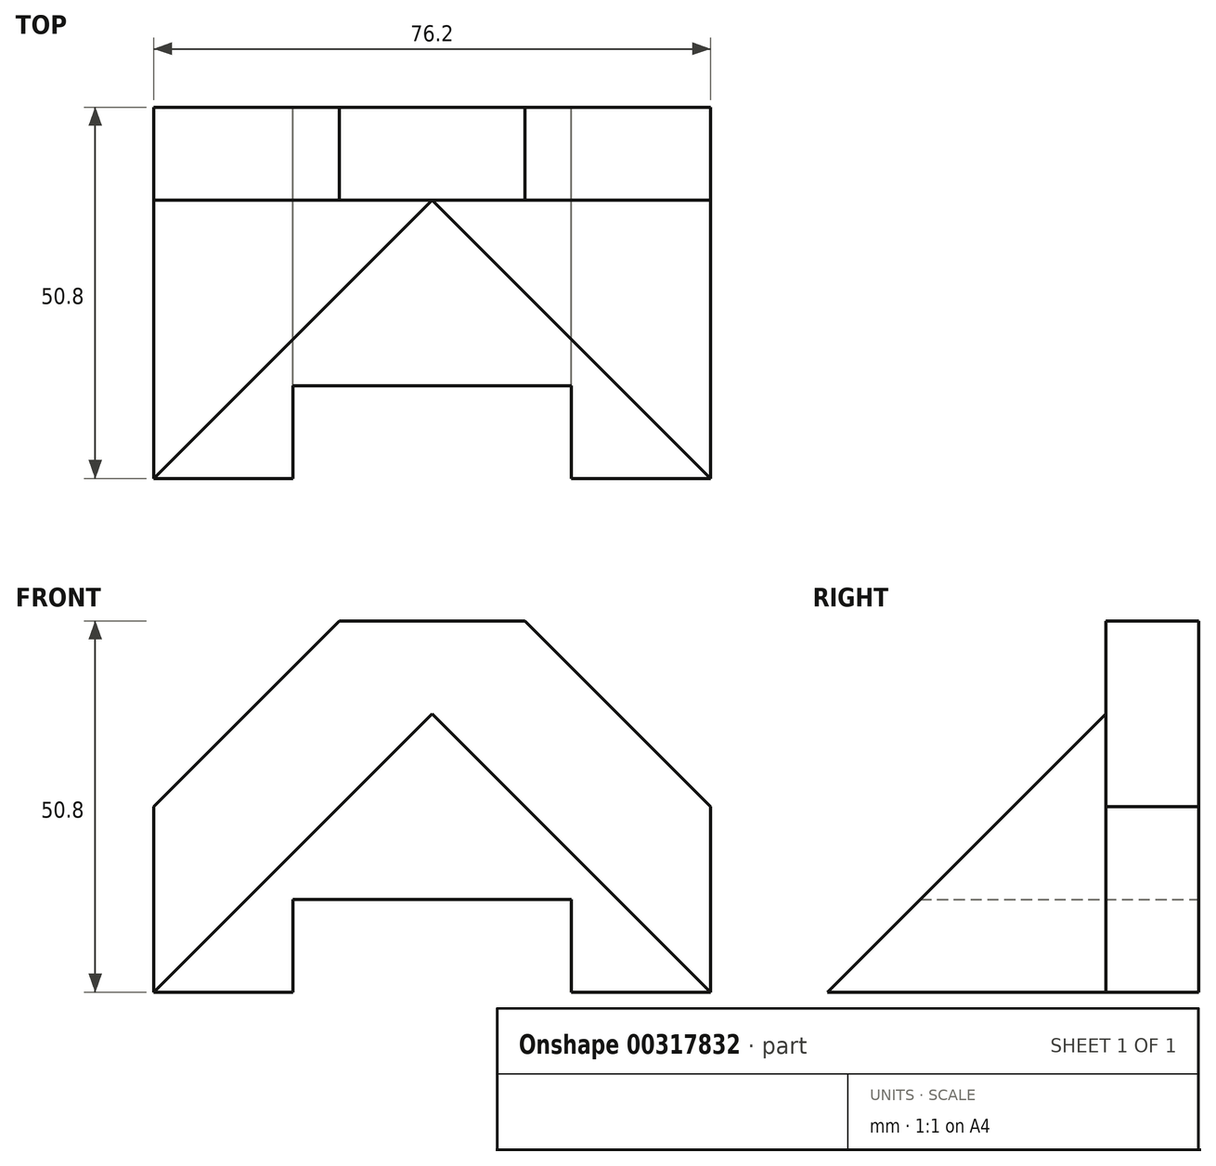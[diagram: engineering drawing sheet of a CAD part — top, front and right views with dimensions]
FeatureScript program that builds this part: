
annotation { "Feature Type Name" : "Feature", "Feature Type Description" : "" }
export const myFeature = defineFeature(function(context is Context, id is Id, definition is map)
    precondition{}
    {
        {
            var Q0;
            Q0=qCreatedBy(makeId("Top.planeOp"),FACE);
            var sketch = newSketch(context, id + "F0", { "sketchPlane" : qUnion([Q0])});
            skLineSegment(sketch, "E0", {"start": v(0, 0) * mm, "end": v(0, 50.8) * mm});
            skLineSegment(sketch, "E1", {"start": v(0, 50.8) * mm, "end": v(76.2, 50.8) * mm});
            skLineSegment(sketch, "E2", {"start": v(76.2, 50.8) * mm, "end": v(76.2, 0) * mm});
            skLineSegment(sketch, "E3", {"start": v(76.2, 0) * mm, "end": v(0, 0) * mm});
            skLineSegment(sketch, "E4", {"start": v(0, 38.1) * mm, "end": v(76.2, 38.1) * mm});
            skSolve(sketch);
        }
        {
            var Q0;
            {var subQ0=sQuery(id+"F0.wireOp",EDGE,"E1");Q0=makeQuery(id+"F0.imprint","IMPRINT",FACE,{"disambiguationData":[TD([[makeQuery(id+"F0.imprint","IMPRINT",EDGE,{"derivedFrom":subQ0}),-1.0]])]});}
            extrude(context, id + "F1", {"entities" : qUnion([Q0]), "depth" : 50.8 * mm});
        }
        {
            var Q0;
            Q0=makeQuery(id+"F1.opExtrude","SWEPT_FACE",FACE,{"disambiguationData":[OSD([sQuery(id+"F0.wireOp",EDGE,"E1")])]});
            var sketch = newSketch(context, id + "F2", { "sketchPlane" : qUnion([Q0])});
            skLineSegment(sketch, "E5", {"start": v(-25.4, 50.8) * mm, "end": v(0, 25.4) * mm});
            skLineSegment(sketch, "E6", {"start": v(0, 25.4) * mm, "end": v(0, 50.8) * mm});
            skLineSegment(sketch, "E7", {"start": v(0, 50.8) * mm, "end": v(-25.4, 50.8) * mm});
            skLineSegment(sketch, "E8", {"start": v(-50.8, 50.8) * mm, "end": v(-76.2, 50.8) * mm});
            skLineSegment(sketch, "E9", {"start": v(-76.2, 50.8) * mm, "end": v(-76.2, 25.4) * mm});
            skLineSegment(sketch, "E10", {"start": v(-76.2, 25.4) * mm, "end": v(-50.8, 50.8) * mm});
            skSolve(sketch);
        }
        {
            var Q0;
            Q0 = qSketchRegion(id + "F2", true);
            extrude(context, id + "F3", {"entities" : qUnion([Q0]), "operationType" : NewBodyOperationType.REMOVE, "endBound" : BoundingType.THROUGH_ALL, "oppositeDirection" : true, "depth" : 25.4 * mm});
        }
        {
            var Q0;
            {var subQ0=sQuery(id+"F0.wireOp",EDGE,"E3");Q0=makeQuery(id+"F0.imprint","IMPRINT",FACE,{"disambiguationData":[TD([[makeQuery(id+"F0.imprint","IMPRINT",EDGE,{"derivedFrom":subQ0}),-1.0]])]});}
            extrude(context, id + "F4", {"entities" : qUnion([Q0]), "operationType" : NewBodyOperationType.ADD, "depth" : 38.1 * mm});
        }
        {
            var Q0;
            {var subQ0=sQuery(id+"F0.wireOp",EDGE,"E2");Q0=makeQuery(id+"F4.boolean.opBoolean","MERGE",FACE,{"derivedFrom":[makeQuery(id+"F1.opExtrude","SWEPT_FACE",FACE,{"disambiguationData":[OSD([subQ0])]}),makeQuery(id+"F4.opExtrude","SWEPT_FACE",FACE,{"disambiguationData":[OSD([subQ0])]})]});}
            var sketch = newSketch(context, id + "F5", { "sketchPlane" : qUnion([Q0])});
            skLineSegment(sketch, "E11", {"start": v(38.1, 38.1) * mm, "end": v(0, 0) * mm});
            skLineSegment(sketch, "E12", {"start": v(0, 0) * mm, "end": v(38.1, 0) * mm});
            skLineSegment(sketch, "E13", {"start": v(38.1, 0) * mm, "end": v(38.1, 38.1) * mm});
            skSolve(sketch);
        }
        {
            var Q0;
            Q0=makeQuery(id+"F5.imprint","IMPRINT",FACE,{"disambiguationData":[TD([[makeQuery(id+"F5.imprint","IMPRINT",EDGE,{"derivedFrom":sQuery(id+"F5.wireOp",EDGE,"E11")}),-1.0]])]});
            extrude(context, id + "F6", {"entities" : qUnion([Q0]), "operationType" : NewBodyOperationType.REMOVE, "endBound" : BoundingType.THROUGH_ALL, "oppositeDirection" : true, "depth" : 25.4 * mm});
        }
        {
            var Q0;
            Q0=makeQuery(id+"F1.opExtrude","SWEPT_FACE",FACE,{"disambiguationData":[OSD([sQuery(id+"F0.wireOp",EDGE,"E1")])]});
            var sketch = newSketch(context, id + "F7", { "sketchPlane" : qUnion([Q0])});
            skLineSegment(sketch, "E14", {"start": v(-57.15, 0) * mm, "end": v(-19.05, 0) * mm});
            skLineSegment(sketch, "E15", {"start": v(-19.05, 0) * mm, "end": v(-19.05, 12.7) * mm});
            skLineSegment(sketch, "E16", {"start": v(-19.05, 12.7) * mm, "end": v(-57.15, 12.7) * mm});
            skLineSegment(sketch, "E17", {"start": v(-57.15, 12.7) * mm, "end": v(-57.15, 0) * mm});
            skSolve(sketch);
        }
        {
            var Q0;
            Q0=makeQuery(id+"F7.imprint","IMPRINT",FACE,{"disambiguationData":[TD([[makeQuery(id+"F7.imprint","IMPRINT",EDGE,{"derivedFrom":sQuery(id+"F7.wireOp",EDGE,"E14")}),-1.0]])]});
            extrude(context, id + "F8", {"entities" : qUnion([Q0]), "operationType" : NewBodyOperationType.REMOVE, "endBound" : BoundingType.THROUGH_ALL, "oppositeDirection" : true, "depth" : 25.4 * mm});
        }
        {
            var Q0;
            Q0=qCreatedBy(makeId("Front.planeOp"),FACE);
            var sketch = newSketch(context, id + "F9", { "sketchPlane" : qUnion([Q0])});
            skLineSegment(sketch, "E18", {"start": v(0, 0) * mm, "end": v(76.2, 0) * mm});
            skLineSegment(sketch, "E19", {"start": v(76.2, 0) * mm, "end": v(76.2, 38.1) * mm});
            skLineSegment(sketch, "E20", {"start": v(76.2, 38.1) * mm, "end": v(0, 38.1) * mm});
            skLineSegment(sketch, "E21", {"start": v(0, 38.1) * mm, "end": v(0, 0) * mm});
            skLineSegment(sketch, "E22", {"start": v(0, 0) * mm, "end": v(38.1, 38.1) * mm});
            skLineSegment(sketch, "E23", {"start": v(38.1, 38.1) * mm, "end": v(76.2, 0) * mm});
            skSolve(sketch);
        }
        {
            var Q0;
            {var subQ0=sQuery(id+"F9.wireOp",EDGE,"E21");Q0=makeQuery(id+"F9.imprint","IMPRINT",FACE,{"disambiguationData":[TD([[makeQuery(id+"F9.imprint","IMPRINT",EDGE,{"derivedFrom":subQ0}),1.0]])]});}
            var Q1;
            {var subQ0=sQuery(id+"F9.wireOp",EDGE,"E19");Q1=makeQuery(id+"F9.imprint","IMPRINT",FACE,{"disambiguationData":[TD([[makeQuery(id+"F9.imprint","IMPRINT",EDGE,{"derivedFrom":subQ0}),1.0]])]});}
            extrude(context, id + "F10", {"entities" : qUnion([Q0, Q1]), "operationType" : NewBodyOperationType.REMOVE, "oppositeDirection" : true, "depth" : 38.1 * mm});
        }
    });
